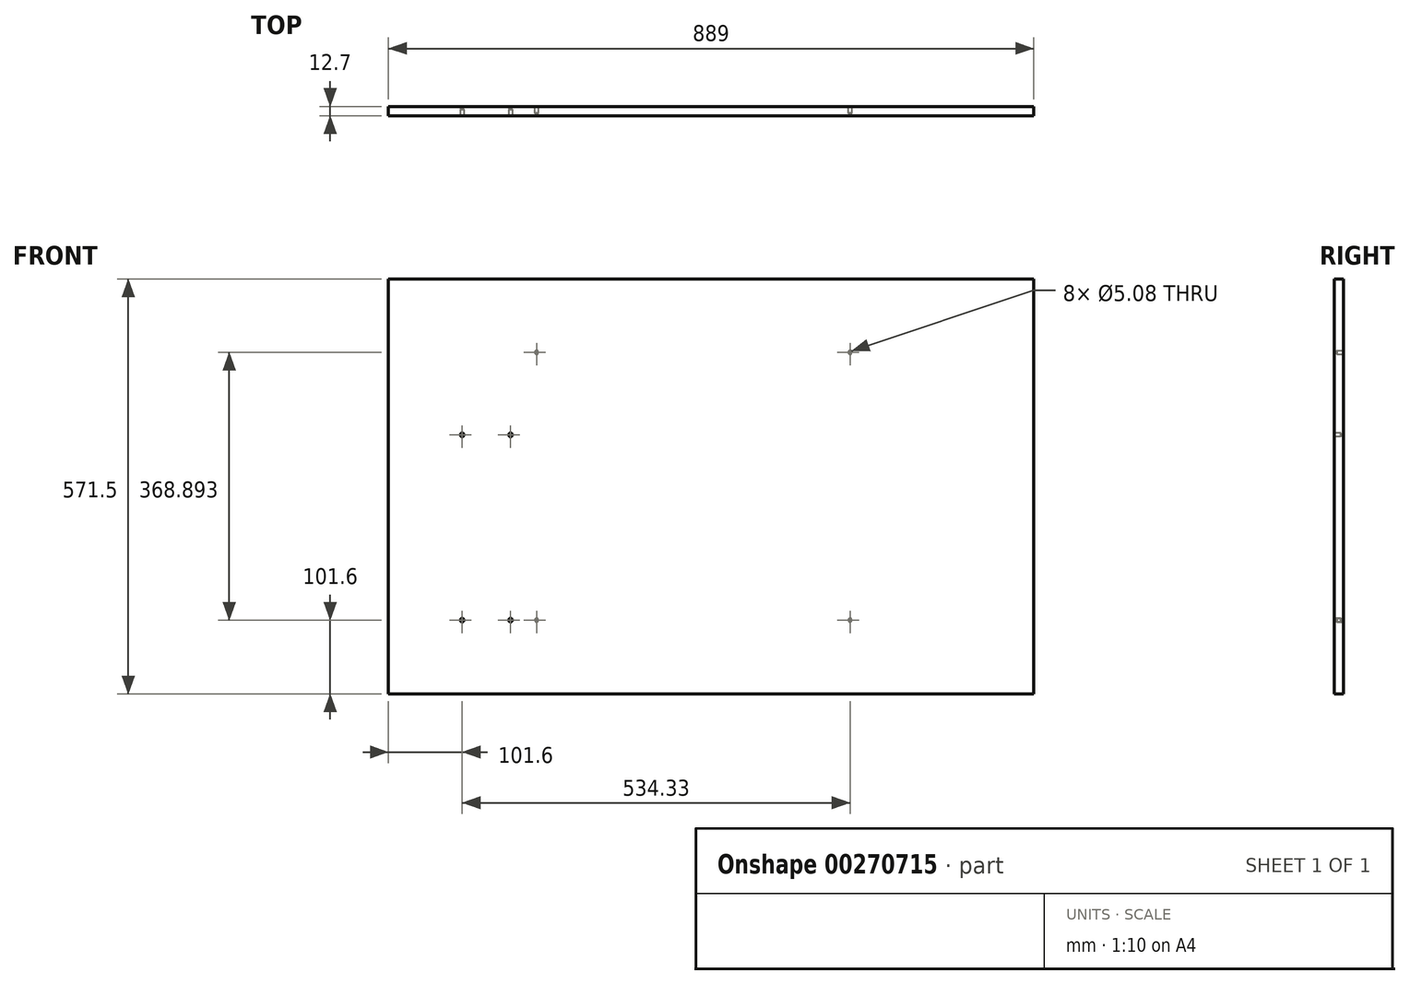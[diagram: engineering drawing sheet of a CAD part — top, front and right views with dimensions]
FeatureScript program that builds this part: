
annotation { "Feature Type Name" : "Feature", "Feature Type Description" : "" }
export const myFeature = defineFeature(function(context is Context, id is Id, definition is map)
    precondition{}
    {
        {
            var Q0;
            Q0=qCreatedBy(makeId("Front.planeOp"),FACE);
            var sketch = newSketch(context, id + "F0", { "sketchPlane" : qUnion([Q0])});
            skLineSegment(sketch, "E0.bottom", {"start": v(0, 0) * mm, "end": v(889, 0) * mm});
            skLineSegment(sketch, "E0.top", {"start": v(0, 571.5) * mm, "end": v(889, 571.5) * mm});
            skLineSegment(sketch, "E0.left", {"start": v(0, 0) * mm, "end": v(0, 571.5) * mm});
            skLineSegment(sketch, "E0.right", {"start": v(889, 0) * mm, "end": v(889, 571.5) * mm});
            skSolve(sketch);
        }
        {
            var Q0;
            Q0 = qSketchRegion(id + "F0", true);
            extrude(context, id + "F1", {"entities" : qUnion([Q0]), "depth" : 12.7 * mm});
        }
        {
            var Q0;
            Q0=makeQuery(id+"F1.opExtrude","CAP_FACE",FACE,{"disambiguationData":[OSD([sQuery(id+"F0.wireOp",EDGE,"E0.bottom"),sQuery(id+"F0.wireOp",EDGE,"E0.top"),sQuery(id+"F0.wireOp",EDGE,"E0.left"),sQuery(id+"F0.wireOp",EDGE,"E0.right")])],"isStart":true});
            var sketch = newSketch(context, id + "F2", { "sketchPlane" : qUnion([Q0])});
            skPoint(sketch, "E1", {"position": v(-204.13, 470.5) * mm});
            skPoint(sketch, "E2", {"position": v(-635.93, 470.5) * mm});
            skPoint(sketch, "E3", {"position": v(-635.93, 101.61) * mm});
            skPoint(sketch, "E4", {"position": v(-204.13, 101.61) * mm});
            skLineSegment(sketch, "E5", {"start": v(-889, 0) * mm, "end": v(-889, 285.75) * mm});
            skLineSegment(sketch, "E6", {"start": v(-889, 285.75) * mm, "end": v(-863.6, 285.75) * mm});
            skLineSegment(sketch, "E7", {"start": v(-863.6, 285.75) * mm, "end": v(-863.6, 0) * mm});
            skSolve(sketch);
        }
        {
            var Q0;
            Q0=sQuery(id+"F2.wireOp",VERTEX,"E2");
            var Q1;
            Q1=sQuery(id+"F2.wireOp",VERTEX,"E3");
            var Q2;
            Q2=sQuery(id+"F2.wireOp",VERTEX,"E4");
            var Q3;
            Q3=sQuery(id+"F2.wireOp",VERTEX,"E1");
            var Q4;
            Q4=makeQuery(id+"F1.opExtrude","SWEPT_BODY",BODY,{"disambiguationData":[OSD([sQuery(id+"F0.wireOp",EDGE,"E0.bottom"),sQuery(id+"F0.wireOp",EDGE,"E0.top"),sQuery(id+"F0.wireOp",EDGE,"E0.left"),sQuery(id+"F0.wireOp",EDGE,"E0.right")])]});
            hole(context, id + "F3", {"style" : HoleStyle.SIMPLE, "endStyle" : HoleEndStyle.BLIND, "holeDiameter" : 5.08 * mm, "holeDepth" : 8.9 * mm, "tappedDepth" : 12.7 * mm, "tapClearance" : 3, "locations" : qUnion([Q0, Q1, Q2, Q3]), "scope" : qUnion([Q4])});
        }
        {
            var Q0;
            Q0=makeQuery(id+"F1.opExtrude","CAP_FACE",FACE,{"disambiguationData":[OSD([sQuery(id+"F0.wireOp",EDGE,"E0.bottom"),sQuery(id+"F0.wireOp",EDGE,"E0.top"),sQuery(id+"F0.wireOp",EDGE,"E0.left"),sQuery(id+"F0.wireOp",EDGE,"E0.right")])],"isStart":false});
            var sketch = newSketch(context, id + "F4", { "sketchPlane" : qUnion([Q0])});
            skPoint(sketch, "E8", {"position": v(101.6, 101.6) * mm});
            skPoint(sketch, "E9", {"position": v(168.28, 101.6) * mm});
            skPoint(sketch, "E10", {"position": v(101.6, 356.84) * mm});
            skPoint(sketch, "E11", {"position": v(168.28, 356.84) * mm});
            skLineSegment(sketch, "E12", {"start": v(101.6, 356.84) * mm, "end": v(168.28, 356.84) * mm});
            skSolve(sketch);
        }
        {
            var Q0;
            Q0=sQuery(id+"F4.wireOp",VERTEX,"E8");
            var Q1;
            Q1=sQuery(id+"F4.wireOp",VERTEX,"E9");
            var Q2;
            Q2=sQuery(id+"F4.wireOp",VERTEX,"E10");
            var Q3;
            Q3=sQuery(id+"F4.wireOp",VERTEX,"E11");
            var Q4;
            Q4=makeQuery(id+"F1.opExtrude","SWEPT_BODY",BODY,{"disambiguationData":[OSD([sQuery(id+"F0.wireOp",EDGE,"E0.bottom"),sQuery(id+"F0.wireOp",EDGE,"E0.top"),sQuery(id+"F0.wireOp",EDGE,"E0.left"),sQuery(id+"F0.wireOp",EDGE,"E0.right")])]});
            hole(context, id + "F5", {"style" : HoleStyle.SIMPLE, "endStyle" : HoleEndStyle.BLIND, "holeDiameter" : 5.08 * mm, "holeDepth" : 8.9 * mm, "tappedDepth" : 12.7 * mm, "tapClearance" : 3, "locations" : qUnion([Q0, Q1, Q2, Q3]), "scope" : qUnion([Q4])});
        }
    });
